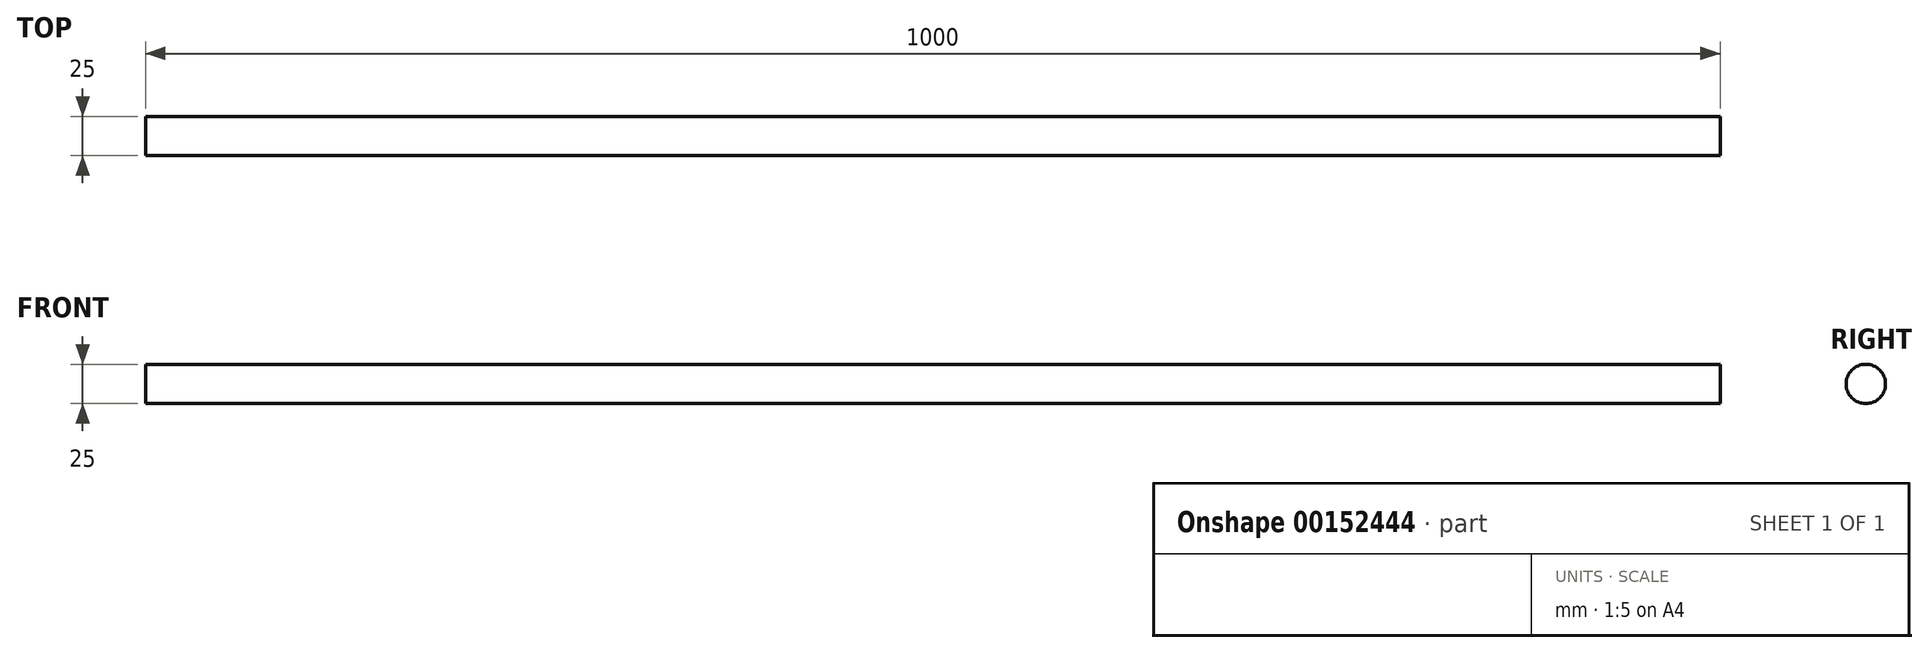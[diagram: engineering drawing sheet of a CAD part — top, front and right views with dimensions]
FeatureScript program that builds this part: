
annotation { "Feature Type Name" : "Feature", "Feature Type Description" : "" }
export const myFeature = defineFeature(function(context is Context, id is Id, definition is map)
    precondition{}
    {
        {
            var Q0;
            Q0=qCreatedBy(makeId("Right.planeOp"),FACE);
            var sketch = newSketch(context, id + "F0", { "sketchPlane" : qUnion([Q0])});
            skCircle(sketch, "E0", {"center": v(0, 0) * mm, "radius": 12.5 * mm});
            skSolve(sketch);
        }
        {
            var Q0;
            Q0=makeQuery(id+"F0.imprint","IMPRINT",FACE,{"disambiguationData":[TD([[makeQuery(id+"F0.imprint","IMPRINT",EDGE,{"derivedFrom":sQuery(id+"F0.wireOp",EDGE,"E0")}),1.0]])]});
            extrude(context, id + "F1", {"entities" : qUnion([Q0]), "depth" : 1000 * mm});
        }
    });
